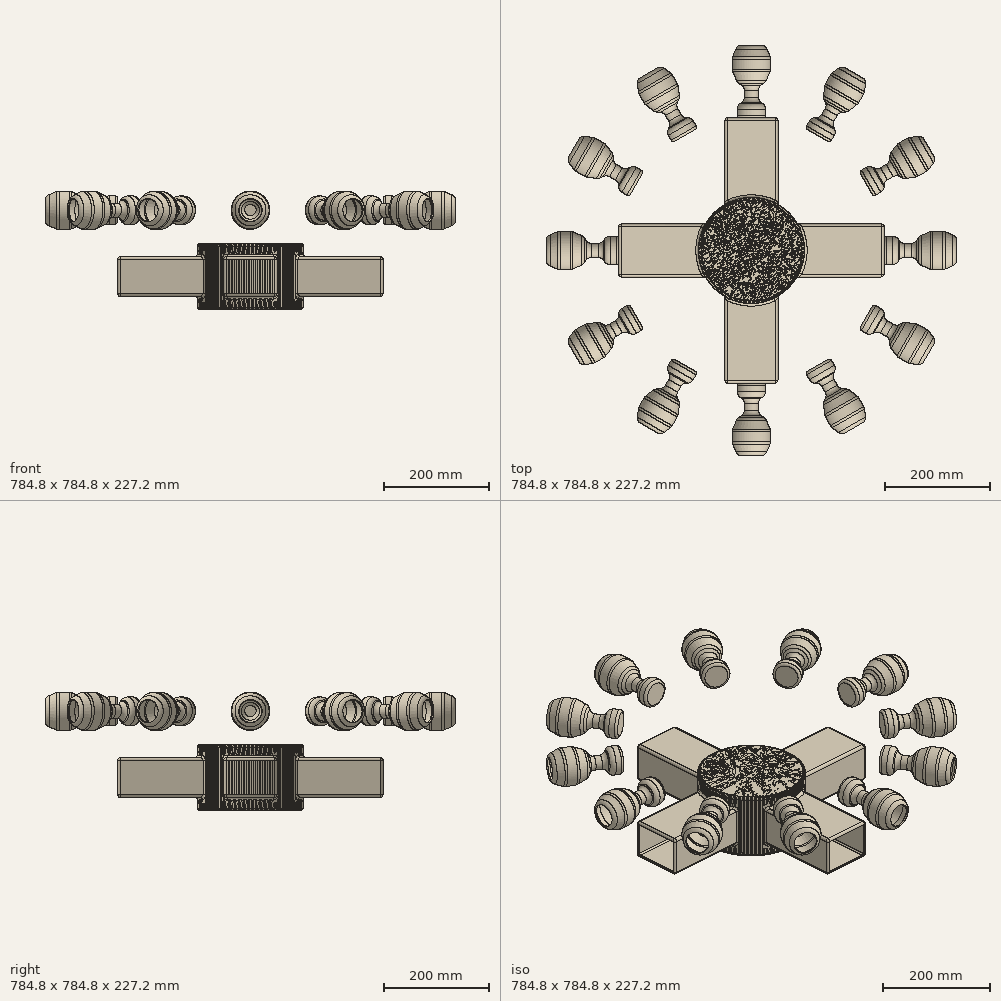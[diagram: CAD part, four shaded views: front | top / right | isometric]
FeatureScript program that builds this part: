
annotation { "Feature Type Name" : "Feature", "Feature Type Description" : "" }
export const myFeature = defineFeature(function(context is Context, id is Id, definition is map)
    precondition{}
    {
        {
            var Q0;
            Q0=qCreatedBy(makeId("Front.planeOp"),FACE);
            var sketch = newSketch(context, id + "F0", { "sketchPlane" : qUnion([Q0])});
            skLineSegment(sketch, "E0.bottom", {"start": v(-50.8, 38.1) * mm, "end": v(50.8, 38.1) * mm});
            skLineSegment(sketch, "E0.top", {"start": v(-50.8, -38.1) * mm, "end": v(50.8, -38.1) * mm});
            skLineSegment(sketch, "E0.left", {"start": v(-50.8, 38.1) * mm, "end": v(-50.8, -38.1) * mm});
            skLineSegment(sketch, "E0.right", {"start": v(50.8, 38.1) * mm, "end": v(50.8, -38.1) * mm});
            skPoint(sketch, "E0.middle", {"position": v(0, 0) * mm});
            skSolve(sketch);
        }
        {
            var Q0;
            Q0=makeQuery(id+"F0.imprint","IMPRINT",FACE,{"disambiguationData":[TD([[makeQuery(id+"F0.imprint","IMPRINT",EDGE,{"derivedFrom":sQuery(id+"F0.wireOp",EDGE,"E0.bottom")}),-1.0]])]});
            extrude(context, id + "F1", {"entities" : qUnion([Q0]), "depth" : 254 * mm});
        }
        {
            var Q0;
            Q0=makeQuery(id+"F1.opExtrude","CAP_FACE",FACE,{"disambiguationData":[OSD([sQuery(id+"F0.wireOp",EDGE,"E0.bottom"),sQuery(id+"F0.wireOp",EDGE,"E0.top"),sQuery(id+"F0.wireOp",EDGE,"E0.left"),sQuery(id+"F0.wireOp",EDGE,"E0.right")])],"isStart":false});
            var sketch = newSketch(context, id + "F2", { "sketchPlane" : qUnion([Q0])});
            skLineSegment(sketch, "E1", {"start": v(0, 38.1) * mm, "end": v(0, -38.1) * mm, "construction": true});
            skSolve(sketch);
        }
        {
            var Q0;
            Q0=makeQuery(id+"F2.imprint","IMPRINT",FACE,{"disambiguationData":[TD([[makeQuery(id+"F2.imprint","IMPRINT",EDGE,{"derivedFrom":makeQuery(id+"F1.opExtrude","CAP_EDGE",EDGE,{"disambiguationData":[OSD([sQuery(id+"F0.wireOp",EDGE,"E0.bottom")])],"isStart":false})}),-1.0]])]});
            var sketch = newSketch(context, id + "F3", { "sketchPlane" : qUnion([Q0])});
            skLineSegment(sketch, "E2.0", {"start": v(0, 38.1) * mm, "end": v(0, -38.1) * mm});
            skLineSegment(sketch, "E3.bottom", {"start": v(0, 63.5) * mm, "end": v(101.6, 63.5) * mm});
            skLineSegment(sketch, "E3.top", {"start": v(0, -63.5) * mm, "end": v(101.6, -63.5) * mm});
            skLineSegment(sketch, "E3.left", {"start": v(0, 63.5) * mm, "end": v(0, -63.5) * mm});
            skLineSegment(sketch, "E3.right", {"start": v(101.6, 63.5) * mm, "end": v(101.6, -63.5) * mm});
            skSolve(sketch);
        }
        {
            var Q0;
            Q0 = qSketchRegion(id + "F3", true);
            var Q1;
            Q1=sQuery(id+"F3.wireOp",EDGE,"E3.left");
            revolve(context, id + "F4", {"operationType" : NewBodyOperationType.ADD, "entities" : qUnion([Q0]), "axis" : qUnion([Q1]), "revolveType" : RevolveType.FULL});
        }
        {
            var Q0;
            Q0=makeQuery(id+"F4.boolean.opBoolean","INTERSECT",EDGE,{"derivedFrom":[makeQuery(id+"F1.opExtrude","SWEPT_FACE",FACE,{"disambiguationData":[OSD([sQuery(id+"F0.wireOp",EDGE,"E0.right")])]}),makeQuery(id+"F4.opRevolve","SWEPT_FACE",FACE,{"disambiguationData":[OSD([sQuery(id+"F3.wireOp",EDGE,"E3.right")])]})]});
            var Q1;
            Q1=makeQuery(id+"F4.boolean.opBoolean","INTERSECT",EDGE,{"derivedFrom":[makeQuery(id+"F1.opExtrude","SWEPT_FACE",FACE,{"disambiguationData":[OSD([sQuery(id+"F0.wireOp",EDGE,"E0.bottom")])]}),makeQuery(id+"F4.opRevolve","SWEPT_FACE",FACE,{"disambiguationData":[OSD([sQuery(id+"F3.wireOp",EDGE,"E3.right")])]})]});
            var Q2;
            Q2=makeQuery(id+"F4.opRevolve","SWEPT_FACE",FACE,{"disambiguationData":[OSD([sQuery(id+"F3.wireOp",EDGE,"E3.right")])]});
            var Q3;
            Q3=makeQuery(id+"F4.boolean.opBoolean","INTERSECT",EDGE,{"derivedFrom":[makeQuery(id+"F1.opExtrude","SWEPT_FACE",FACE,{"disambiguationData":[OSD([sQuery(id+"F0.wireOp",EDGE,"E0.top")])]}),makeQuery(id+"F4.opRevolve","SWEPT_FACE",FACE,{"disambiguationData":[OSD([sQuery(id+"F3.wireOp",EDGE,"E3.right")])]})]});
            var Q4;
            Q4=makeQuery(id+"F1.opExtrude","CAP_EDGE",EDGE,{"disambiguationData":[OSD([sQuery(id+"F0.wireOp",EDGE,"E0.bottom")])],"isStart":true});
            var Q5;
            Q5=makeQuery(id+"F1.opExtrude","CAP_FACE",FACE,{"disambiguationData":[OSD([sQuery(id+"F0.wireOp",EDGE,"E0.bottom"),sQuery(id+"F0.wireOp",EDGE,"E0.top"),sQuery(id+"F0.wireOp",EDGE,"E0.left"),sQuery(id+"F0.wireOp",EDGE,"E0.right")])],"isStart":true});
            var Q6;
            Q6=makeQuery(id+"F1.opExtrude","SWEPT_EDGE",EDGE,{"disambiguationData":[OSD([sQuery(id+"F0.wireOp",EDGE,"E0.bottom"),sQuery(id+"F0.wireOp",EDGE,"E0.right")])]});
            var Q7;
            Q7=makeQuery(id+"F1.opExtrude","SWEPT_EDGE",EDGE,{"disambiguationData":[OSD([sQuery(id+"F0.wireOp",EDGE,"E0.bottom"),sQuery(id+"F0.wireOp",EDGE,"E0.left")])]});
            var Q8;
            Q8=makeQuery(id+"F1.opExtrude","SWEPT_EDGE",EDGE,{"disambiguationData":[OSD([sQuery(id+"F0.wireOp",EDGE,"E0.top"),sQuery(id+"F0.wireOp",EDGE,"E0.right")])]});
            var Q9;
            Q9=makeQuery(id+"F1.opExtrude","SWEPT_FACE",FACE,{"disambiguationData":[OSD([sQuery(id+"F0.wireOp",EDGE,"E0.top")])]});
            fillet(context, id + "F5", {"entities" : qUnion([Q0, Q1, Q2, Q3, Q4, Q5, Q6, Q7, Q8, Q9]), "radius" : 5.08 * mm, "tangentPropagation" : true, "allowEdgeOverflow" : false});
        }
        {
            var Q0;
            Q0=makeQuery(id+"F1.opExtrude","CAP_FACE",FACE,{"disambiguationData":[OSD([sQuery(id+"F0.wireOp",EDGE,"E0.bottom"),sQuery(id+"F0.wireOp",EDGE,"E0.top"),sQuery(id+"F0.wireOp",EDGE,"E0.left"),sQuery(id+"F0.wireOp",EDGE,"E0.right")])],"isStart":true});
            shell(context, id + "F6", {"entities" : qUnion([Q0]), "thickness" : 2.54 * mm});
        }
        {
            var Q0;
            Q0=makeQuery(id+"F4.opRevolve","SWEPT_FACE",FACE,{"disambiguationData":[OSD([sQuery(id+"F3.wireOp",EDGE,"E3.bottom")])]});
            var sketch = newSketch(context, id + "F7", { "sketchPlane" : qUnion([Q0])});
            skCircle(sketch, "E4", {"center": v(0, -203.2) * mm, "radius": 12.7 * mm});
            skSolve(sketch);
        }
        {
            var Q0;
            Q0=makeQuery(id+"F7.imprint","IMPRINT",FACE,{"disambiguationData":[TD([[makeQuery(id+"F7.imprint","IMPRINT",EDGE,{"derivedFrom":sQuery(id+"F7.wireOp",EDGE,"E4")}),1.0]])]});
            extrude(context, id + "F8", {"entities" : qUnion([Q0]), "operationType" : NewBodyOperationType.REMOVE, "endBound" : BoundingType.THROUGH_ALL, "oppositeDirection" : true, "depth" : 25.4 * mm});
        }
        {
            var Q0;
            Q0=makeQuery(id+"F1.opExtrude","SWEPT_BODY",BODY,{"disambiguationData":[OSD([sQuery(id+"F0.wireOp",EDGE,"E0.bottom"),sQuery(id+"F0.wireOp",EDGE,"E0.top"),sQuery(id+"F0.wireOp",EDGE,"E0.left"),sQuery(id+"F0.wireOp",EDGE,"E0.right")])]});
            var Q1;
            Q1=sQuery(id+"F2.wireOp",EDGE,"E1");
            circularPattern(context, id + "F9", {"entities" : qUnion([Q0]), "axis" : qUnion([Q1]), "angle" : 360 * degree, "instanceCount" : 4, "equalSpace" : true});
        }
        {
            var Q0;
            Q0=qCreatedBy(makeId("Top.planeOp"),FACE);
            cPlane(context, id + "F10", {"entities" : qUnion([Q0]), "cplaneType" : CPlaneType.OFFSET, "offset" : 127 * mm, "width" : 152.4 * mm, "height" : 152.4 * mm});
        }
        {
            var Q0;
            Q0=qCreatedBy(id+"F10.planeOp",FACE);
            var sketch = newSketch(context, id + "F11", { "sketchPlane" : qUnion([Q0])});
            skLineSegment(sketch, "E5", {"start": v(0, 0) * mm, "end": v(-27.49, 0) * mm});
            skLineSegment(sketch, "E6", {"start": v(-27.49, 0) * mm, "end": v(-27.49, 16.06) * mm});
            skLineSegment(sketch, "E7", {"start": v(-21.74, 26.69) * mm, "end": v(-19.17, 28.37) * mm});
            skLineSegment(sketch, "E8", {"start": v(-13.42, 39) * mm, "end": v(-13.42, 51.64) * mm});
            skLineSegment(sketch, "E9", {"start": v(-18.63, 61.9) * mm, "end": v(-27.49, 68.37) * mm});
            skLineSegment(sketch, "E10", {"start": v(-27.49, 68.37) * mm, "end": v(-35.73, 88.4) * mm});
            skLineSegment(sketch, "E11", {"start": v(-36.7, 93.23) * mm, "end": v(-36.7, 115.06) * mm});
            skLineSegment(sketch, "E12", {"start": v(-36.7, 115.06) * mm, "end": v(-29.66, 131.45) * mm});
            skLineSegment(sketch, "E13", {"start": v(-22.29, 138.4) * mm, "end": v(0, 146.42) * mm});
            skLineSegment(sketch, "E14", {"start": v(0, 146.42) * mm, "end": v(0, 0) * mm});
            skPoint(sketch, "E15.visualSharp", {"position": v(-27.49, 136.53) * mm});
            skArc(sketch, "E15.filletArc", {"start": v(-22.29, 138.4) * mm, "mid": v(-26.7, 135.7) * mm, "end": v(-29.66, 131.45) * mm});
            skPoint(sketch, "E16.visualSharp", {"position": v(-36.7, 90.71) * mm});
            skArc(sketch, "E16.filletArc", {"start": v(-36.7, 93.23) * mm, "mid": v(-36.45, 90.76) * mm, "end": v(-35.73, 88.4) * mm});
            skPoint(sketch, "E17.visualSharp", {"position": v(-13.42, 58.1) * mm});
            skArc(sketch, "E17.filletArc", {"start": v(-13.42, 51.64) * mm, "mid": v(-14.8, 57.4) * mm, "end": v(-18.63, 61.9) * mm});
            skPoint(sketch, "E18.visualSharp", {"position": v(-13.42, 32.13) * mm});
            skArc(sketch, "E18.filletArc", {"start": v(-19.17, 28.37) * mm, "mid": v(-14.95, 32.95) * mm, "end": v(-13.42, 39) * mm});
            skPoint(sketch, "E19.visualSharp", {"position": v(-27.49, 22.93) * mm});
            skArc(sketch, "E19.filletArc", {"start": v(-21.74, 26.69) * mm, "mid": v(-25.96, 22.1) * mm, "end": v(-27.49, 16.06) * mm});
            skSolve(sketch);
        }
        {
            var Q0;
            Q0=makeQuery(id+"F11.imprint","IMPRINT",FACE,{"disambiguationData":[TD([[makeQuery(id+"F11.imprint","IMPRINT",EDGE,{"derivedFrom":sQuery(id+"F11.wireOp",EDGE,"E5")}),-1.0]])]});
            var Q1;
            Q1=sQuery(id+"F11.wireOp",EDGE,"E14");
            revolve(context, id + "F12", {"entities" : qUnion([Q0]), "axis" : qUnion([Q1]), "revolveType" : RevolveType.FULL});
        }
        {
            var Q0;
            Q0=makeQuery(id+"F12.opRevolve","SWEPT_FACE",FACE,{"disambiguationData":[OSD([sQuery(id+"F11.wireOp",EDGE,"E13")])]});
            shell(context, id + "F13", {"entities" : qUnion([Q0]), "thickness" : 2.54 * mm});
        }
        {
            var Q0;
            Q0=makeQuery(id+"F12.opRevolve","SWEPT_EDGE",EDGE,{"disambiguationData":[OSD([sQuery(id+"F11.wireOp",EDGE,"E5"),sQuery(id+"F11.wireOp",EDGE,"E6")])]});
            fillet(context, id + "F14", {"entities" : qUnion([Q0]), "radius" : 5.08 * mm, "tangentPropagation" : true, "allowEdgeOverflow" : false});
        }
        {
            var Q0;
            Q0=makeQuery(id+"F12.opRevolve","SWEPT_EDGE",EDGE,{"disambiguationData":[OSD([sQuery(id+"F11.wireOp",EDGE,"E9"),sQuery(id+"F11.wireOp",EDGE,"E10")])]});
            fillet(context, id + "F15", {"entities" : qUnion([Q0]), "radius" : 12.7 * mm, "tangentPropagation" : true, "allowEdgeOverflow" : false});
        }
        {
            var Q0;
            Q0=makeQuery(id+"F12.opRevolve","SWEPT_EDGE",EDGE,{"disambiguationData":[OSD([sQuery(id+"F11.wireOp",EDGE,"E11"),sQuery(id+"F11.wireOp",EDGE,"E12")])]});
            fillet(context, id + "F16", {"entities" : qUnion([Q0]), "radius" : 12.7 * mm, "tangentPropagation" : true, "allowEdgeOverflow" : false});
        }
        {
            var Q0;
            Q0=makeQuery(id+"F9.opPattern","COPY",FACE,{"derivedFrom":makeQuery(id+"F4.opRevolve","SWEPT_FACE",FACE,{"disambiguationData":[OSD([sQuery(id+"F3.wireOp",EDGE,"E3.bottom")])]}),"instanceName":"3"});
            var sketch = newSketch(context, id + "F17", { "sketchPlane" : qUnion([Q0])});
            skPoint(sketch, "E20", {"position": v(0, -254) * mm});
            skSolve(sketch);
        }
        {
            var Q0;
            Q0=qCreatedBy(makeId("Right.planeOp"),FACE);
            var sketch = newSketch(context, id + "F18", { "sketchPlane" : qUnion([Q0])});
            skPoint(sketch, "E21.0", {"position": v(-254, 63.5) * mm});
            skLineSegment(sketch, "E22", {"start": v(-254, 63.5) * mm, "end": v(-254, -103.07) * mm});
            skSolve(sketch);
        }
        {
            var Q0;
            Q0=makeQuery(id+"F12.opRevolve","SWEPT_BODY",BODY,{"disambiguationData":[OSD([sQuery(id+"F11.wireOp",EDGE,"E5"),sQuery(id+"F11.wireOp",EDGE,"E6"),sQuery(id+"F11.wireOp",EDGE,"E7"),sQuery(id+"F11.wireOp",EDGE,"E8"),sQuery(id+"F11.wireOp",EDGE,"E9"),sQuery(id+"F11.wireOp",EDGE,"E10"),sQuery(id+"F11.wireOp",EDGE,"E11"),sQuery(id+"F11.wireOp",EDGE,"E12"),sQuery(id+"F11.wireOp",EDGE,"E13"),sQuery(id+"F11.wireOp",EDGE,"E14"),sQuery(id+"F11.wireOp",EDGE,"E15.filletArc"),sQuery(id+"F11.wireOp",EDGE,"E16.filletArc"),sQuery(id+"F11.wireOp",EDGE,"E17.filletArc"),sQuery(id+"F11.wireOp",EDGE,"E18.filletArc"),sQuery(id+"F11.wireOp",EDGE,"E19.filletArc")])]});
            var Q1;
            Q1=sQuery(id+"F18.wireOp",EDGE,"E22");
            circularPattern(context, id + "F19", {"entities" : qUnion([Q0]), "axis" : qUnion([Q1]), "angle" : 360 * degree, "instanceCount" : 12, "equalSpace" : true});
        }
    });
